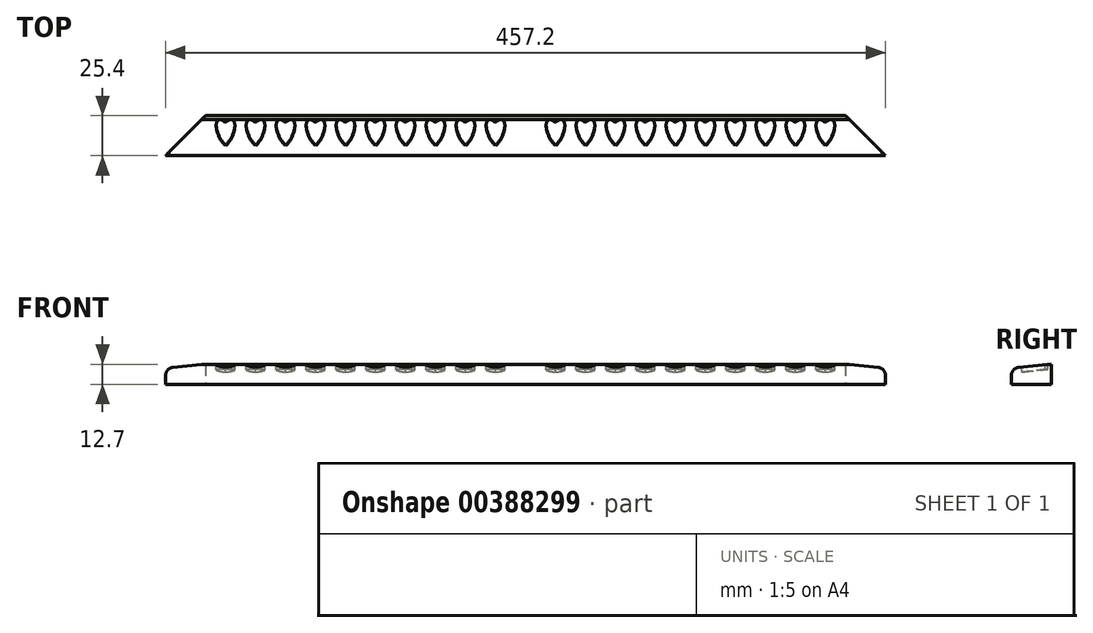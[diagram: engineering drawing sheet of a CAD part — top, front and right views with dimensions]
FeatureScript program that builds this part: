
annotation { "Feature Type Name" : "Feature", "Feature Type Description" : "" }
export const myFeature = defineFeature(function(context is Context, id is Id, definition is map)
    precondition{}
    {
        {
            var Q0;
            Q0=qCreatedBy(makeId("Top.planeOp"),FACE);
            var sketch = newSketch(context, id + "F0", { "sketchPlane" : qUnion([Q0])});
            skLineSegment(sketch, "E0.bottom", {"start": v(-228.6, 12.7) * mm, "end": v(228.6, 12.7) * mm});
            skLineSegment(sketch, "E0.top", {"start": v(-228.6, -12.7) * mm, "end": v(228.6, -12.7) * mm});
            skLineSegment(sketch, "E0.left", {"start": v(-228.6, 12.7) * mm, "end": v(-228.6, -12.7) * mm});
            skLineSegment(sketch, "E0.right", {"start": v(228.6, 12.7) * mm, "end": v(228.6, -12.7) * mm});
            skPoint(sketch, "E0.middle", {"position": v(0, 0) * mm});
            skLineSegment(sketch, "E1", {"start": v(-228.6, -12.7) * mm, "end": v(-203.2, 12.7) * mm});
            skLineSegment(sketch, "E2.MirrorCS", {"start": v(228.6, -12.7) * mm, "end": v(203.2, 12.7) * mm});
            skSolve(sketch);
        }
        {
            var Q0;
            Q0=makeQuery(id+"F0.imprint","IMPRINT",FACE,{"disambiguationData":[TD([[makeQuery(id+"F0.imprint","IMPRINT",EDGE,{"derivedFrom":sQuery(id+"F0.wireOp",EDGE,"E0.top")}),1.0]])]});
            extrude(context, id + "F1", {"entities" : qUnion([Q0]), "depth" : 12.7 * mm});
        }
        {
            var Q0;
            Q0=makeQuery(id+"F1.opExtrude","CAP_EDGE",EDGE,{"disambiguationData":[OSD([sQuery(id+"F0.wireOp",EDGE,"E0.top")])],"isStart":false});
            chamfer(context, id + "F2", {"entities" : qUnion([Q0]), "chamferType" : ChamferType.TWO_OFFSETS, "width1" : 2.54 * mm, "oppositeDirection" : true, "width2" : 22.86 * mm, "tangentPropagation" : true});
        }
        {
            var Q0;
            {var subQ0=sQuery(id+"F0.wireOp",EDGE,"E0.top");Q0=makeQuery(id+"F2.opChamfer","BLEND_EDGE",EDGE,{"blendedFrom":[makeQuery(id+"F1.opExtrude","CAP_EDGE",EDGE,{"disambiguationData":[OSD([subQ0])],"isStart":false}),makeQuery(id+"F1.opExtrude","SWEPT_FACE",FACE,{"disambiguationData":[OSD([subQ0])]})],"blendedInto":[makeQuery(id+"F1.opExtrude","SWEPT_FACE",FACE,{"disambiguationData":[OSD([subQ0])]})]});}
            fillet(context, id + "F3", {"entities" : qUnion([Q0]), "radius" : 5.08 * mm, "tangentPropagation" : true, "allowEdgeOverflow" : false});
        }
        {
            var Q0;
            Q0=makeQuery(id+"F2.opChamfer","BLEND_FACE",FACE,{"disambiguationData":[OSD([sQuery(id+"F0.wireOp",EDGE,"E0.top")])]});
            var sketch = newSketch(context, id + "F4", { "sketchPlane" : qUnion([Q0])});
            skLineSegment(sketch, "E3.bottom", {"start": v(-6.1, 11.5) * mm, "end": v(6.1, 11.5) * mm});
            skLineSegment(sketch, "E3.top", {"start": v(-6.1, -6.95) * mm, "end": v(6.1, -6.95) * mm});
            skLineSegment(sketch, "E3.left", {"start": v(-6.1, 11.5) * mm, "end": v(-6.1, -6.95) * mm});
            skLineSegment(sketch, "E3.right", {"start": v(6.1, 11.5) * mm, "end": v(6.1, -6.95) * mm});
            skPoint(sketch, "E3.middle", {"position": v(0, 2.27) * mm});
            skPoint(sketch, "E3.middle.positionSnap0", {"position": v(-214.91, 2.27) * mm});
            skPoint(sketch, "E3.centerSnap0", {"position": v(-214.91, 2.27) * mm});
            skEllipticalArc(sketch, "E4", {});
            skEllipticalArc(sketch, "E5", {});
            skEllipticalArc(sketch, "E6.0.1.0", {});
            skEllipticalArc(sketch, "E6.0.1.1", {});
            skEllipticalArc(sketch, "E6.1.0.0", {});
            skEllipticalArc(sketch, "E6.1.0.1", {});
            skEllipticalArc(sketch, "E6.1.1.0", {});
            skEllipticalArc(sketch, "E6.1.1.1", {});
            skEllipticalArc(sketch, "E6.2.0.0", {});
            skEllipticalArc(sketch, "E6.2.0.1", {});
            skEllipticalArc(sketch, "E6.2.1.0", {});
            skEllipticalArc(sketch, "E6.2.1.1", {});
            skEllipticalArc(sketch, "E6.3.0.0", {});
            skEllipticalArc(sketch, "E6.3.0.1", {});
            skEllipticalArc(sketch, "E6.3.1.0", {});
            skEllipticalArc(sketch, "E6.3.1.1", {});
            skEllipticalArc(sketch, "E6.4.0.0", {});
            skEllipticalArc(sketch, "E6.4.0.1", {});
            skEllipticalArc(sketch, "E6.4.1.0", {});
            skEllipticalArc(sketch, "E6.4.1.1", {});
            skEllipticalArc(sketch, "E6.5.0.0", {});
            skEllipticalArc(sketch, "E6.5.0.1", {});
            skEllipticalArc(sketch, "E6.5.1.0", {});
            skEllipticalArc(sketch, "E6.5.1.1", {});
            skEllipticalArc(sketch, "E6.6.0.0", {});
            skEllipticalArc(sketch, "E6.6.0.1", {});
            skEllipticalArc(sketch, "E6.6.1.0", {});
            skEllipticalArc(sketch, "E6.6.1.1", {});
            skEllipticalArc(sketch, "E6.7.0.0", {});
            skEllipticalArc(sketch, "E6.7.0.1", {});
            skEllipticalArc(sketch, "E6.7.1.0", {});
            skEllipticalArc(sketch, "E6.7.1.1", {});
            skEllipticalArc(sketch, "E6.8.0.0", {});
            skEllipticalArc(sketch, "E6.8.0.1", {});
            skEllipticalArc(sketch, "E6.8.1.0", {});
            skEllipticalArc(sketch, "E6.8.1.1", {});
            skEllipticalArc(sketch, "E6.9.0.0", {});
            skEllipticalArc(sketch, "E6.9.0.1", {});
            skEllipticalArc(sketch, "E6.9.1.0", {});
            skEllipticalArc(sketch, "E6.9.1.1", {});
            skLineSegment(sketch, "E6.direction1", {"start": v(0.03, -5.24) * mm, "end": v(19.08, -5.24) * mm, "construction": true});
            skLineSegment(sketch, "E6.direction2", {"start": v(0.03, -5.24) * mm, "end": v(-190.47, -5.24) * mm, "construction": true});
            skEllipticalArc(sketch, "E7.0.10.0", {});
            skEllipticalArc(sketch, "E7.4.10.0", {});
            skEllipticalArc(sketch, "E7.0.10.1", {});
            skEllipticalArc(sketch, "E7.4.10.1", {});
            const initialGuessF4  = {"E4": [0, 0.002273408694540999, 0.43307739417193414, 0.9013567388427556, 0.010033, 0.004445, 3.972859161622577, 0.8312665080327042], "E5": [0, 0.002273408694540999, -0.4406524803443906, 0.8976777771373963, 0.010033, 0.004445, 5.451918799146794, 2.3103261455570094], "E6.0.1.0": [-0.1905, 0.0022734086945409753, -0.44065248034439053, 0.8976777771373962, 0.010033, 0.004445, 5.451918799146802, 2.3103261455570094], "E6.0.1.1": [-0.1905, 0.0022734086945409753, 0.43307739417193414, 0.9013567388427556, 0.010033, 0.004445, 3.97285916162258, 0.8312665080327717], "E6.1.0.0": [0.01905, 0.0022734086945409987, -0.44065248034439053, 0.8976777771373962, 0.010033, 0.004445, 5.451918799146794, 2.31032614555701], "E6.1.0.1": [0.01905, 0.002273408694540999, 0.4330773941719341, 0.9013567388427556, 0.010033, 0.004445, 3.972859161622577, 0.831266508032704], "E6.1.1.0": [-0.17145, 0.0022734086945409753, -0.44065248034439053, 0.8976777771373962, 0.010033, 0.004445, 5.451918799146805, 2.3103261455570068], "E6.1.1.1": [-0.17145, 0.0022734086945409753, 0.43307739417193414, 0.9013567388427556, 0.010033, 0.004445, 3.9728591616225777, 0.8312665080327742], "E6.2.0.0": [0.0381, 0.002273408694540999, -0.44065248034439053, 0.8976777771373962, 0.010033, 0.004445, 5.451918799146795, 2.31032614555701], "E6.2.0.1": [0.0381, 0.002273408694540999, 0.4330773941719341, 0.9013567388427556, 0.010033, 0.004445, 3.9728591616225772, 0.8312665080327044], "E6.2.1.0": [-0.1524, 0.0022734086945409753, -0.44065248034439053, 0.8976777771373962, 0.010033, 0.004445, 5.451918799146802, 2.3103261455570094], "E6.2.1.1": [-0.1524, 0.0022734086945409753, 0.43307739417193414, 0.9013567388427556, 0.010033, 0.004445, 3.9728591616225803, 0.8312665080327717], "E6.3.0.0": [0.05715, 0.002273408694540999, -0.44065248034439053, 0.8976777771373962, 0.010033, 0.004445, 5.451918799146796, 2.3103261455570094], "E6.3.0.1": [0.05715, 0.0022734086945409987, 0.4330773941719341, 0.9013567388427556, 0.010033, 0.004445, 3.9728591616225772, 0.8312665080327044], "E6.3.1.0": [-0.13335, 0.0022734086945409753, -0.44065248034439053, 0.8976777771373962, 0.010033, 0.004445, 5.451918799146805, 2.3103261455570094], "E6.3.1.1": [-0.13335, 0.0022734086945409753, 0.43307739417193414, 0.9013567388427556, 0.010033, 0.004445, 3.9728591616225803, 0.8312665080327742], "E6.4.0.0": [0.0762, 0.002273408694540999, -0.44065248034439053, 0.8976777771373962, 0.010033, 0.004445, 5.451918799146795, 2.31032614555701], "E6.4.0.1": [0.0762, 0.0022734086945409996, 0.4330773941719341, 0.9013567388427556, 0.010033, 0.004445, 3.972859161622577, 0.8312665080327044], "E6.4.1.0": [-0.1143, 0.0022734086945409753, -0.44065248034439053, 0.8976777771373962, 0.010033, 0.004445, 5.451918799146804, 2.310326145557008], "E6.4.1.1": [-0.1143, 0.0022734086945409753, 0.43307739417193414, 0.9013567388427556, 0.010033, 0.004445, 3.972859161622579, 0.8312665080327729], "E6.5.0.0": [0.09525, 0.002273408694540999, -0.44065248034439053, 0.8976777771373962, 0.010033, 0.004445, 5.451918799146793, 2.310326145557011], "E6.5.0.1": [0.09525, 0.0022734086945409987, 0.4330773941719341, 0.9013567388427556, 0.010033, 0.004445, 3.9728591616225772, 0.8312665080327044], "E6.5.1.0": [-0.09525, 0.0022734086945409753, -0.44065248034439053, 0.8976777771373962, 0.010033, 0.004445, 5.451918799146804, 2.310326145557008], "E6.5.1.1": [-0.09525, 0.0022734086945409753, 0.43307739417193414, 0.9013567388427556, 0.010033, 0.004445, 3.972859161622579, 0.8312665080327729], "E6.6.0.0": [0.1143, 0.002273408694540999, -0.44065248034439053, 0.8976777771373962, 0.010033, 0.004445, 5.451918799146795, 2.31032614555701], "E6.6.0.1": [0.1143, 0.002273408694540999, 0.4330773941719341, 0.9013567388427556, 0.010033, 0.004445, 3.972859161622578, 0.8312665080327031], "E6.6.1.0": [-0.0762, 0.0022734086945409753, -0.44065248034439053, 0.8976777771373962, 0.010033, 0.004445, 5.451918799146804, 2.310326145557008], "E6.6.1.1": [-0.0762, 0.0022734086945409753, 0.43307739417193414, 0.9013567388427556, 0.010033, 0.004445, 3.972859161622579, 0.8312665080327729], "E6.7.0.0": [0.13335, 0.002273408694540999, -0.44065248034439053, 0.8976777771373962, 0.010033, 0.004445, 5.451918799146791, 2.310326145557011], "E6.7.0.1": [0.13335, 0.0022734086945409987, 0.4330773941719341, 0.9013567388427556, 0.010033, 0.004445, 3.972859161622576, 0.8312665080327031], "E6.7.1.0": [-0.05715, 0.0022734086945409753, -0.44065248034439053, 0.8976777771373962, 0.010033, 0.004445, 5.451918799146805, 2.3103261455570094], "E6.7.1.1": [-0.05715, 0.0022734086945409753, 0.43307739417193414, 0.9013567388427556, 0.010033, 0.004445, 3.9728591616225803, 0.8312665080327742], "E6.8.0.0": [0.1524, 0.002273408694540999, -0.44065248034439053, 0.8976777771373962, 0.010033, 0.004445, 5.451918799146793, 2.3103261455570085], "E6.8.0.1": [0.1524, 0.002273408694540999, 0.4330773941719341, 0.9013567388427556, 0.010033, 0.004445, 3.972859161622576, 0.8312665080327031], "E6.8.1.0": [-0.0381, 0.0022734086945409753, -0.44065248034439053, 0.8976777771373962, 0.010033, 0.004445, 5.451918799146805, 2.3103261455570094], "E6.8.1.1": [-0.0381, 0.0022734086945409753, 0.43307739417193414, 0.9013567388427556, 0.010033, 0.004445, 3.9728591616225803, 0.8312665080327742], "E6.9.0.0": [0.17145, 0.002273408694540999, -0.44065248034439053, 0.8976777771373962, 0.010033, 0.004445, 5.451918799146793, 2.3103261455570085], "E6.9.0.1": [0.17145, 0.002273408694540999, 0.4330773941719341, 0.9013567388427556, 0.010033, 0.004445, 3.9728591616225732, 0.8312665080327056], "E6.9.1.0": [-0.01905, 0.0022734086945409753, -0.44065248034439053, 0.8976777771373962, 0.010033, 0.004445, 5.451918799146805, 2.3103261455570094], "E6.9.1.1": [-0.01905, 0.0022734086945409753, 0.43307739417193414, 0.9013567388427556, 0.010033, 0.004445, 3.9728591616225803, 0.8312665080327742], "E7.0.10.0": [0.1905, 0.002273408694540999, -0.4406524803443905, 0.897677777137396, 0.010033, 0.004445, 5.451918799146792, 2.3103261455570085], "E7.4.10.0": [0.1905, 0.002273408694540999, 0.43307739417193414, 0.9013567388427556, 0.010033, 0.004445, 3.9728591616225755, 0.8312665080327029], "E7.0.10.1": [0, 0.0022734086945409753, -0.44065248034439053, 0.8976777771373962, 0.010033, 0.004445, 5.451918799146802, 2.3103261455570068], "E7.4.10.1": [0, 0.0022734086945409753, 0.43307739417193414, 0.9013567388427556, 0.010033, 0.004445, 3.9728591616225777, 0.8312665080327717]};
            skSetInitialGuess(sketch, initialGuessF4);
            skSolve(sketch);
        }
        {
            var Q0;
            {var subQ0=sQuery(id+"F4.wireOp",EDGE,"E6.0.1.0");Q0=makeQuery(id+"F4.imprint","IMPRINT",FACE,{"disambiguationData":[TD([[makeQuery(id+"F4.imprint","IMPRINT",EDGE,{"derivedFrom":subQ0}),1.0]])]});}
            var Q1;
            {var subQ0=sQuery(id+"F4.wireOp",EDGE,"E6.1.1.0");Q1=makeQuery(id+"F4.imprint","IMPRINT",FACE,{"disambiguationData":[TD([[makeQuery(id+"F4.imprint","IMPRINT",EDGE,{"derivedFrom":subQ0}),1.0]])]});}
            var Q2;
            {var subQ0=sQuery(id+"F4.wireOp",EDGE,"E6.2.1.0");Q2=makeQuery(id+"F4.imprint","IMPRINT",FACE,{"disambiguationData":[TD([[makeQuery(id+"F4.imprint","IMPRINT",EDGE,{"derivedFrom":subQ0}),1.0]])]});}
            var Q3;
            {var subQ0=sQuery(id+"F4.wireOp",EDGE,"E6.3.1.0");Q3=makeQuery(id+"F4.imprint","IMPRINT",FACE,{"disambiguationData":[TD([[makeQuery(id+"F4.imprint","IMPRINT",EDGE,{"derivedFrom":subQ0}),1.0]])]});}
            var Q4;
            {var subQ0=sQuery(id+"F4.wireOp",EDGE,"E6.4.1.0");Q4=makeQuery(id+"F4.imprint","IMPRINT",FACE,{"disambiguationData":[TD([[makeQuery(id+"F4.imprint","IMPRINT",EDGE,{"derivedFrom":subQ0}),1.0]])]});}
            var Q5;
            {var subQ0=sQuery(id+"F4.wireOp",EDGE,"E6.5.1.0");Q5=makeQuery(id+"F4.imprint","IMPRINT",FACE,{"disambiguationData":[TD([[makeQuery(id+"F4.imprint","IMPRINT",EDGE,{"derivedFrom":subQ0}),1.0]])]});}
            var Q6;
            {var subQ0=sQuery(id+"F4.wireOp",EDGE,"E6.6.1.0");Q6=makeQuery(id+"F4.imprint","IMPRINT",FACE,{"disambiguationData":[TD([[makeQuery(id+"F4.imprint","IMPRINT",EDGE,{"derivedFrom":subQ0}),1.0]])]});}
            var Q7;
            {var subQ0=sQuery(id+"F4.wireOp",EDGE,"E6.7.1.0");Q7=makeQuery(id+"F4.imprint","IMPRINT",FACE,{"disambiguationData":[TD([[makeQuery(id+"F4.imprint","IMPRINT",EDGE,{"derivedFrom":subQ0}),1.0]])]});}
            var Q8;
            {var subQ0=sQuery(id+"F4.wireOp",EDGE,"E6.8.1.0");Q8=makeQuery(id+"F4.imprint","IMPRINT",FACE,{"disambiguationData":[TD([[makeQuery(id+"F4.imprint","IMPRINT",EDGE,{"derivedFrom":subQ0}),1.0]])]});}
            var Q9;
            {var subQ0=sQuery(id+"F4.wireOp",EDGE,"E6.1.0.0");Q9=makeQuery(id+"F4.imprint","IMPRINT",FACE,{"disambiguationData":[TD([[makeQuery(id+"F4.imprint","IMPRINT",EDGE,{"derivedFrom":subQ0}),1.0]])]});}
            var Q10;
            {var subQ0=sQuery(id+"F4.wireOp",EDGE,"E6.2.0.0");Q10=makeQuery(id+"F4.imprint","IMPRINT",FACE,{"disambiguationData":[TD([[makeQuery(id+"F4.imprint","IMPRINT",EDGE,{"derivedFrom":subQ0}),1.0]])]});}
            var Q11;
            {var subQ0=sQuery(id+"F4.wireOp",EDGE,"E6.3.0.0");Q11=makeQuery(id+"F4.imprint","IMPRINT",FACE,{"disambiguationData":[TD([[makeQuery(id+"F4.imprint","IMPRINT",EDGE,{"derivedFrom":subQ0}),1.0]])]});}
            var Q12;
            {var subQ0=sQuery(id+"F4.wireOp",EDGE,"E6.4.0.0");Q12=makeQuery(id+"F4.imprint","IMPRINT",FACE,{"disambiguationData":[TD([[makeQuery(id+"F4.imprint","IMPRINT",EDGE,{"derivedFrom":subQ0}),1.0]])]});}
            var Q13;
            {var subQ0=sQuery(id+"F4.wireOp",EDGE,"E6.5.0.0");Q13=makeQuery(id+"F4.imprint","IMPRINT",FACE,{"disambiguationData":[TD([[makeQuery(id+"F4.imprint","IMPRINT",EDGE,{"derivedFrom":subQ0}),1.0]])]});}
            var Q14;
            {var subQ0=sQuery(id+"F4.wireOp",EDGE,"E6.6.0.0");Q14=makeQuery(id+"F4.imprint","IMPRINT",FACE,{"disambiguationData":[TD([[makeQuery(id+"F4.imprint","IMPRINT",EDGE,{"derivedFrom":subQ0}),1.0]])]});}
            var Q15;
            {var subQ0=sQuery(id+"F4.wireOp",EDGE,"E6.7.0.0");Q15=makeQuery(id+"F4.imprint","IMPRINT",FACE,{"disambiguationData":[TD([[makeQuery(id+"F4.imprint","IMPRINT",EDGE,{"derivedFrom":subQ0}),1.0]])]});}
            var Q16;
            {var subQ0=sQuery(id+"F4.wireOp",EDGE,"E6.8.0.0");Q16=makeQuery(id+"F4.imprint","IMPRINT",FACE,{"disambiguationData":[TD([[makeQuery(id+"F4.imprint","IMPRINT",EDGE,{"derivedFrom":subQ0}),1.0]])]});}
            var Q17;
            {var subQ0=sQuery(id+"F4.wireOp",EDGE,"E6.9.0.0");Q17=makeQuery(id+"F4.imprint","IMPRINT",FACE,{"disambiguationData":[TD([[makeQuery(id+"F4.imprint","IMPRINT",EDGE,{"derivedFrom":subQ0}),1.0]])]});}
            var Q18;
            {var subQ4=sQuery(id+"F4.wireOp",EDGE,"E6.9.1.0");Q18=makeQuery(id+"F4.imprint","IMPRINT",FACE,{"disambiguationData":[TD([[makeQuery(id+"F4.imprint","IMPRINT",EDGE,{"derivedFrom":subQ4}),1.0]])]});}
            var Q19;
            {var subQ4=sQuery(id+"F4.wireOp",EDGE,"E7.0.10.1");Q19=makeQuery(id+"F4.imprint","IMPRINT",FACE,{"disambiguationData":[TD([[makeQuery(id+"F4.imprint","IMPRINT",EDGE,{"derivedFrom":subQ4}),1.0]])]});}
            var Q20;
            {var subQ0=sQuery(id+"F4.wireOp",EDGE,"E7.0.10.0");Q20=makeQuery(id+"F4.imprint","IMPRINT",FACE,{"disambiguationData":[TD([[makeQuery(id+"F4.imprint","IMPRINT",EDGE,{"derivedFrom":subQ0}),1.0]])]});}
            extrude(context, id + "F5", {"entities" : qUnion([Q0, Q1, Q2, Q3, Q4, Q5, Q6, Q7, Q8, Q9, Q10, Q11, Q12, Q13, Q14, Q15, Q16, Q17, Q18, Q19, Q20]), "operationType" : NewBodyOperationType.REMOVE, "oppositeDirection" : true, "depth" : 3.17 * mm});
        }
    });
